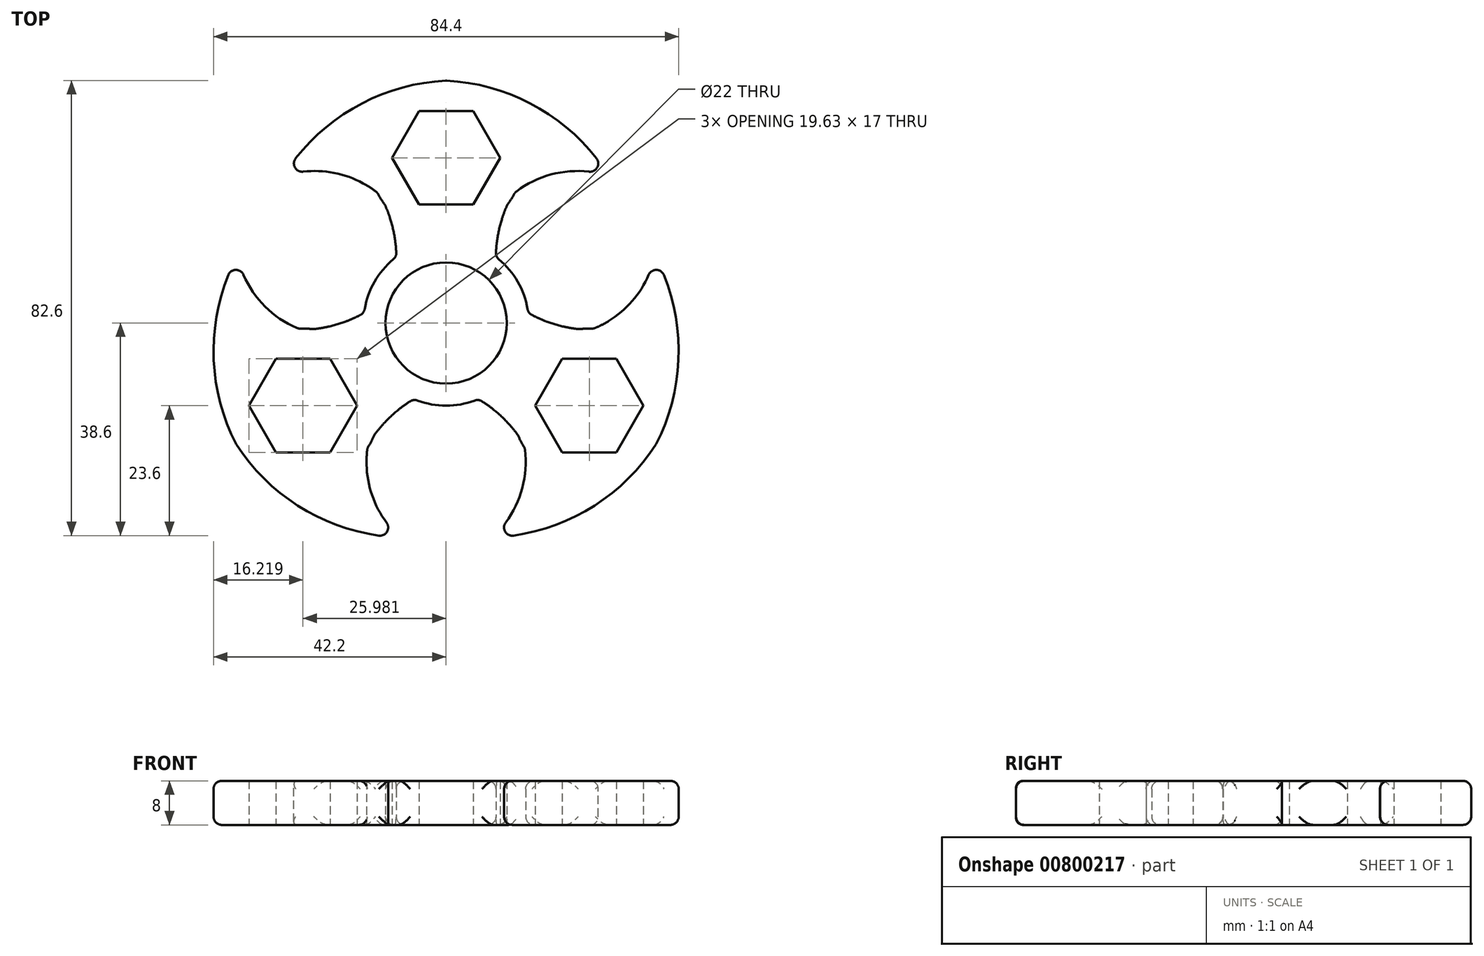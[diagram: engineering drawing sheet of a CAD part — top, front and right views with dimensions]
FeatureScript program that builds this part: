
annotation { "Feature Type Name" : "Feature", "Feature Type Description" : "" }
export const myFeature = defineFeature(function(context is Context, id is Id, definition is map)
    precondition{}
    {
        {
            var Q0;
            Q0=qCreatedBy(makeId("Top.planeOp"),FACE);
            var sketch = newSketch(context, id + "F0", { "sketchPlane" : qUnion([Q0])});
            skCircle(sketch, "E0", {"center": v(0, 0) * mm, "radius": 11 * mm});
            skLineSegment(sketch, "E1", {"start": v(0, 0) * mm, "end": v(0, 30) * mm, "construction": true});
            skCircle(sketch, "E2.cCircle", {"center": v(0, 30) * mm, "radius": 8.5 * mm, "construction": true});
            skLineSegment(sketch, "E2.0", {"start": v(-4.9, 38.5) * mm, "end": v(4.9, 38.5) * mm});
            skLineSegment(sketch, "E2.1", {"start": v(4.9, 38.5) * mm, "end": v(9.81, 30) * mm});
            skLineSegment(sketch, "E2.2", {"start": v(9.81, 30) * mm, "end": v(4.9, 21.5) * mm});
            skLineSegment(sketch, "E2.3", {"start": v(4.9, 21.5) * mm, "end": v(-4.9, 21.5) * mm});
            skLineSegment(sketch, "E2.4", {"start": v(-4.9, 21.5) * mm, "end": v(-9.81, 30) * mm});
            skLineSegment(sketch, "E2.5", {"start": v(-9.81, 30) * mm, "end": v(-4.9, 38.5) * mm});
            skPoint(sketch, "E2.0.midPoint", {"position": v(0, 38.5) * mm});
            skArc(sketch, "E3", {"start": v(-9.03, 11.98) * mm, "mid": v(0, -15) * mm, "end": v(9.03, 11.98) * mm});
            skArc(sketch, "E4", {"start": v(-9.03, 11.98) * mm, "mid": v(-9.59, 16.85) * mm, "end": v(-11.12, 21.5) * mm});
            skArc(sketch, "E5", {"start": v(11.12, 21.5) * mm, "mid": v(11.86, 22.56) * mm, "end": v(12.5, 23.69) * mm});
            skLineSegment(sketch, "E6", {"start": v(0, 21.5) * mm, "end": v(29.55, 26.68) * mm, "construction": true});
            skArc(sketch, "E7", {"start": v(29.55, 26.68) * mm, "mid": v(16.9, 38.97) * mm, "end": v(0, 44) * mm});
            skArc(sketch, "E8", {"start": v(29.55, 26.68) * mm, "mid": v(20.65, 27.32) * mm, "end": v(12.5, 23.69) * mm});
            skArc(sketch, "E9.MirrorCS", {"start": v(-29.55, 26.68) * mm, "mid": v(-20.65, 27.32) * mm, "end": v(-12.5, 23.69) * mm});
            skArc(sketch, "E10.MirrorCS", {"start": v(-29.55, 26.68) * mm, "mid": v(-16.9, 38.97) * mm, "end": v(0, 44) * mm});
            skArc(sketch, "E11.MirrorCS", {"start": v(9.03, 11.98) * mm, "mid": v(9.59, 16.85) * mm, "end": v(11.12, 21.5) * mm});
            skArc(sketch, "E12.trimOffspring", {"start": v(-12.5, 23.69) * mm, "mid": v(-11.86, 22.56) * mm, "end": v(-11.12, 21.5) * mm});
            skArc(sketch, "E13.trimOffspring", {"start": v(2.16, 43.83) * mm, "mid": v(0, 44) * mm, "end": v(-2.16, 43.83) * mm});
            skSolve(sketch);
        }
        {
            var Q0;
            Q0=makeQuery(id+"F0.imprint","IMPRINT",FACE,{"disambiguationData":[TD([[makeQuery(id+"F0.imprint","IMPRINT",EDGE,{"derivedFrom":sQuery(id+"F0.wireOp",EDGE,"E0")}),-1.0]])]});
            extrude(context, id + "F1", {"entities" : qUnion([Q0]), "endBound" : BoundingType.SYMMETRIC, "depth" : 8 * mm, "offsetDistance" : 25 * mm});
        }
        {
            var Q0;
            Q0=makeQuery(id+"F1.opExtrude","SWEPT_FACE",FACE,{"disambiguationData":[OSD([sQuery(id+"F0.wireOp",EDGE,"E10.MirrorCS")])]});
            var Q1;
            Q1=makeQuery(id+"F1.opExtrude","SWEPT_FACE",FACE,{"disambiguationData":[OSD([sQuery(id+"F0.wireOp",EDGE,"E7")])]});
            var Q2;
            Q2=makeQuery(id+"F1.opExtrude","SWEPT_FACE",FACE,{"disambiguationData":[OSD([sQuery(id+"F0.wireOp",EDGE,"E8")])]});
            var Q3;
            Q3=makeQuery(id+"F1.opExtrude","SWEPT_FACE",FACE,{"disambiguationData":[OSD([sQuery(id+"F0.wireOp",EDGE,"E5")])]});
            var Q4;
            Q4=makeQuery(id+"F1.opExtrude","SWEPT_FACE",FACE,{"disambiguationData":[OSD([sQuery(id+"F0.wireOp",EDGE,"E3")])]});
            var Q5;
            Q5=makeQuery(id+"F1.opExtrude","SWEPT_FACE",FACE,{"disambiguationData":[OSD([sQuery(id+"F0.wireOp",EDGE,"E12.trimOffspring")])]});
            fillet(context, id + "F2", {"entities" : qUnion([Q0, Q1, Q2, Q3, Q4, Q5]), "radius" : 1.5 * mm, "tangentPropagation" : true, "allowEdgeOverflow" : false});
        }
        {
            var Q0;
            Q0=makeQuery(id+"F1.opExtrude","SWEPT_BODY",BODY,{"disambiguationData":[OSD([sQuery(id+"F0.wireOp",EDGE,"E0"),sQuery(id+"F0.wireOp",EDGE,"E2.0"),sQuery(id+"F0.wireOp",EDGE,"E2.1"),sQuery(id+"F0.wireOp",EDGE,"E2.2"),sQuery(id+"F0.wireOp",EDGE,"E2.3"),sQuery(id+"F0.wireOp",EDGE,"E2.4"),sQuery(id+"F0.wireOp",EDGE,"E2.5"),sQuery(id+"F0.wireOp",EDGE,"E3"),sQuery(id+"F0.wireOp",EDGE,"E4"),sQuery(id+"F0.wireOp",EDGE,"E5"),sQuery(id+"F0.wireOp",EDGE,"E7"),sQuery(id+"F0.wireOp",EDGE,"E8"),sQuery(id+"F0.wireOp",EDGE,"E9.MirrorCS"),sQuery(id+"F0.wireOp",EDGE,"E10.MirrorCS"),sQuery(id+"F0.wireOp",EDGE,"E11.MirrorCS"),sQuery(id+"F0.wireOp",EDGE,"E12.trimOffspring")])]});
            var Q1;
            Q1=makeQuery(id+"F1.opExtrude","CAP_EDGE",EDGE,{"disambiguationData":[OSD([sQuery(id+"F0.wireOp",EDGE,"E0")])],"isStart":false});
            circularPattern(context, id + "F3", {"operationType" : NewBodyOperationType.ADD, "entities" : qUnion([Q0]), "axis" : qUnion([Q1]), "angle" : 360 * degree, "instanceCount" : 3, "equalSpace" : true});
        }
    });
